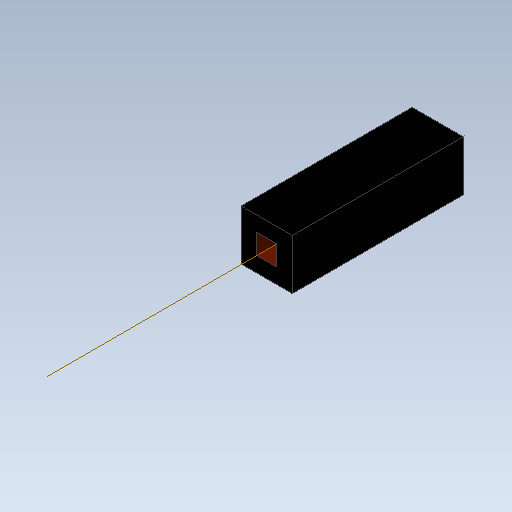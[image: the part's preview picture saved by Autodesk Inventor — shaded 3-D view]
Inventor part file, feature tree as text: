
AUTODESK INVENTOR PART (.ipt)
format: ipt  version: 2020 (Build 240168000, 168)  size: 101,888 bytes
history: native  units: in
note: dims shown in document units (in); Inventor stores cm internally (conversion verified against a paired STEP export)
features: other x2, plane x2
ambient origin geometry x8: Origin, YZ Plane, XZ Plane, XY Plane, X Axis, Y Axis, Z Axis, Center Point
bodies: Solid1 (feature_tree)
feature tree (4):
  other  "Part1"
  other  "Work Axis1"
  plane  "Work Plane1"
  plane  "Work Plane2"
